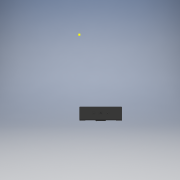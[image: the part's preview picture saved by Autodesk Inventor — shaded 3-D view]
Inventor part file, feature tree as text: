
AUTODESK INVENTOR PART (.ipt)
format: ipt  version: 2018 (Build 220112000, 112)  size: 980,992 bytes
history: native  units: mm
features: sketch x8, extrude x7, fillet x4, other x2
ambient origin geometry x8: Origin, YZ Plane, XZ Plane, XY Plane, X Axis, Y Axis, Z Axis, Center Point
bodies: Solid1 (feature_tree)
feature tree (21):
  other  "34mm_Reflector_Element"
  other  "MeshFeature1"
  extrude  "Extrusion1"  Depth=56.0mm
  extrude  "Extrusion2"  Depth=56.0mm
  sketch  "Sketch3"  dims[d14=3.5mm d15=3.5mm]
  extrude  "Extrusion3"  Depth=3.5mm
  extrude  "Extrusion4"  Depth=3.0mm TaperAngle=0.0deg
  fillet  "Fillet1"  Radius=10.0mm
  extrude  "Extrusion5"  Depth=3.0mm
  extrude  "Extrusion6"  Depth=40.0mm TaperAngle=0.0deg
  extrude  "Extrusion7"  Depth=40.0mm TaperAngle=0.0deg
  fillet  "Fillet2"  Radius=5.0mm
  fillet  "Fillet3"  Radius=3.0mm
  fillet  "Fillet4"  Radius=3.0mm
  sketch  "Sketch1"  dims[d10=55.0mm d11=56.0mm]
  sketch  "Sketch2"  dims[d12=110.0mm d13=56.0mm]
  sketch  "Sketch4"  dims[d17=6.0mm d18=3.0mm d19=0.0mm d20=10.0mm d21=0.0mm]
  sketch  "Sketch5"  dims[d22=15.0mm d23=3.0mm]
  sketch  "Sketch6"  dims[d24=30.0mm d25=40.0mm d26=0.0mm]
  sketch  "Sketch7"  dims[d27=4.0mm d28=40.0mm d29=0.0mm d30=5.0mm d33=3.0mm d34=3.0mm]
  sketch  "Sketch8"  dims[d35=35.0mm d36=0.0mm d37=5.0mm d38=0.0mm d39=5.0mm d40=0.0mm d41=1.0mm d42=1.0mm d43=1.0mm]
